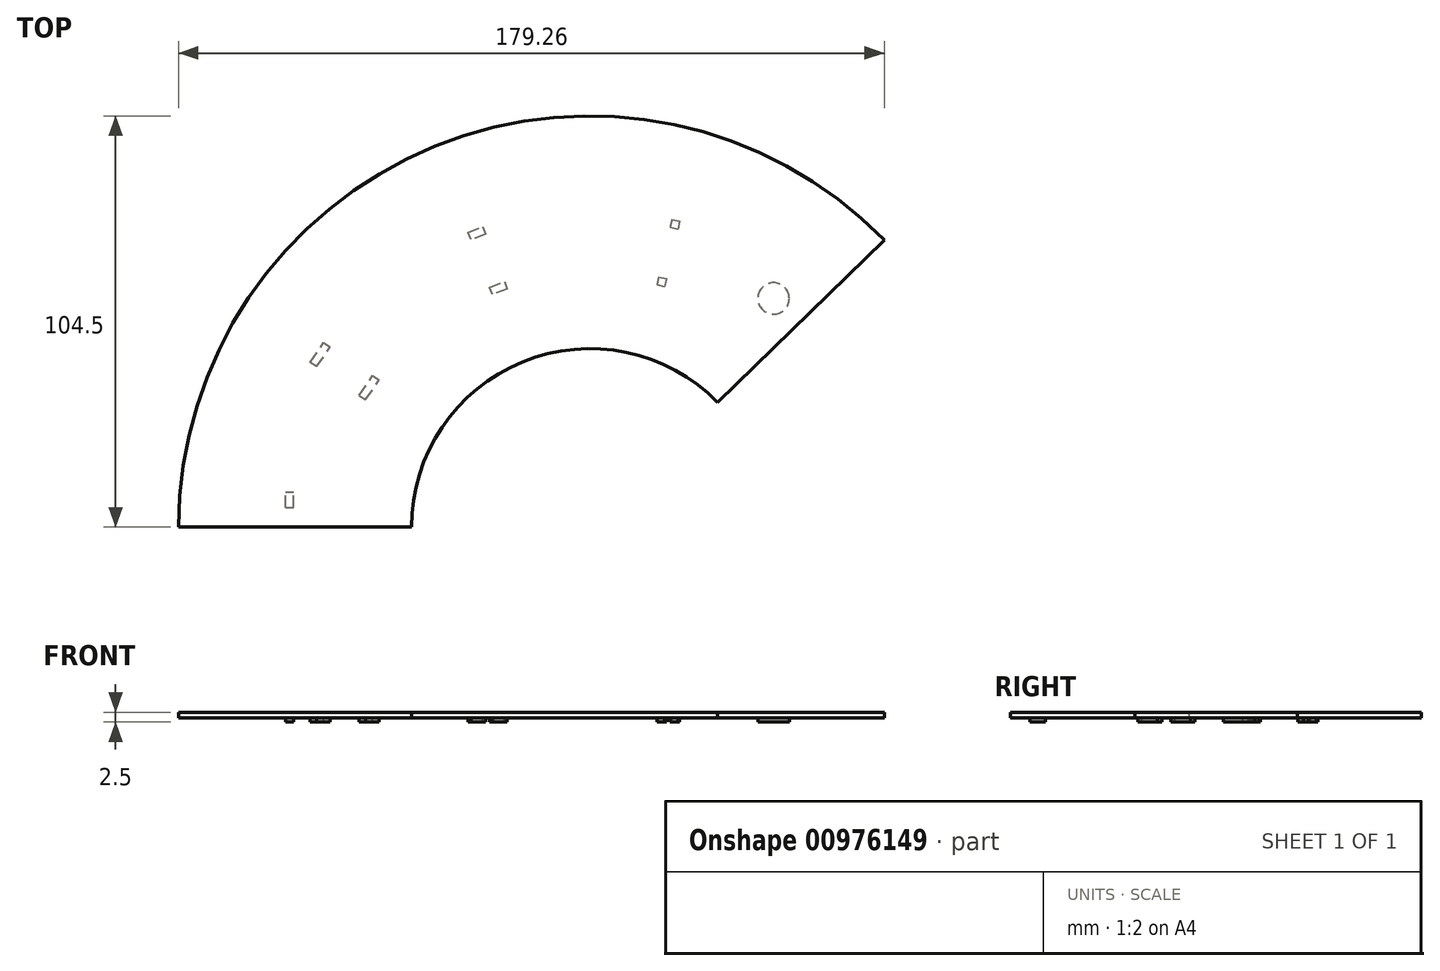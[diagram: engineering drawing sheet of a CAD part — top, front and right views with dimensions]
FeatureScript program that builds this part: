
annotation { "Feature Type Name" : "Feature", "Feature Type Description" : "" }
export const myFeature = defineFeature(function(context is Context, id is Id, definition is map)
    precondition{}
    {
        {
            var Q0;
            Q0=qCreatedBy(makeId("Top.planeOp"),FACE);
            var sketch = newSketch(context, id + "F0", { "sketchPlane" : qUnion([Q0])});
            skArc(sketch, "E0", {"start": v(74.76, 73.01) * mm, "mid": v(-39.42, 96.78) * mm, "end": v(-104.5, 0) * mm});
            skArc(sketch, "E1", {"start": v(32.44, 31.69) * mm, "mid": v(-17.1, 42) * mm, "end": v(-45.35, 0) * mm});
            skLineSegment(sketch, "E2", {"start": v(-45.35, 0) * mm, "end": v(-104.5, 0) * mm});
            skLineSegment(sketch, "E3", {"start": v(32.44, 31.69) * mm, "end": v(74.76, 73.01) * mm});
            skSolve(sketch);
        }
        {
            var Q0;
            Q0=qSketchRegion(id+"F0",true);
            extrude(context, id + "F1", {"entities" : qUnion([Q0]), "depth" : 1.5 * mm, "offsetDistance" : 25 * mm});
        }
        {
            var Q0;
            Q0=makeQuery(id+"F1.opExtrude","CAP_FACE",FACE,{"disambiguationData":[OSD([sQuery(id+"F0.wireOp",EDGE,"E0"),sQuery(id+"F0.wireOp",EDGE,"E1"),sQuery(id+"F0.wireOp",EDGE,"E2"),sQuery(id+"F0.wireOp",EDGE,"E3")])],"isStart":false});
            var sketch = newSketch(context, id + "F2", { "sketchPlane" : qUnion([Q0])});
            skLineSegment(sketch, "E4", {"start": v(-17.1, 42) * mm, "end": v(-39.42, 96.78) * mm});
            skLineSegment(sketch, "E5", {"start": v(-38.13, 24.55) * mm, "end": v(-87.2, 57.58) * mm});
            skLineSegment(sketch, "E6", {"start": v(10.49, 44.12) * mm, "end": v(22.52, 102.04) * mm});
            skLineSegment(sketch, "E7", {"start": v(-54.72, 35.71) * mm, "end": v(-55.84, 34.05) * mm});
            skLineSegment(sketch, "E8", {"start": v(-55.84, 34.05) * mm, "end": v(-57.5, 35.17) * mm});
            skLineSegment(sketch, "E9", {"start": v(-57.5, 35.17) * mm, "end": v(-56.38, 36.83) * mm});
            skLineSegment(sketch, "E10", {"start": v(-56.38, 36.83) * mm, "end": v(-55.27, 38.49) * mm});
            skLineSegment(sketch, "E11", {"start": v(-55.27, 38.49) * mm, "end": v(-53.6, 37.37) * mm});
            skLineSegment(sketch, "E12", {"start": v(-54.72, 35.71) * mm, "end": v(-53.6, 37.37) * mm});
            skLineSegment(sketch, "E13", {"start": v(-67.17, 44.09) * mm, "end": v(-68.29, 42.43) * mm});
            skLineSegment(sketch, "E14", {"start": v(-68.29, 42.43) * mm, "end": v(-69.94, 43.55) * mm});
            skLineSegment(sketch, "E15", {"start": v(-69.94, 43.55) * mm, "end": v(-68.83, 45.2) * mm});
            skLineSegment(sketch, "E16", {"start": v(-68.83, 45.2) * mm, "end": v(-67.71, 46.86) * mm});
            skLineSegment(sketch, "E17", {"start": v(-67.71, 46.86) * mm, "end": v(-66.05, 45.75) * mm});
            skLineSegment(sketch, "E18", {"start": v(-67.17, 44.09) * mm, "end": v(-66.05, 45.75) * mm});
            skLineSegment(sketch, "E19.1.0", {"start": v(-30.98, 74.88) * mm, "end": v(-29.12, 75.62) * mm});
            skLineSegment(sketch, "E19.1.1", {"start": v(-29.12, 75.62) * mm, "end": v(-27.26, 76.35) * mm});
            skLineSegment(sketch, "E19.1.2", {"start": v(-28.39, 73.76) * mm, "end": v(-26.53, 74.5) * mm});
            skLineSegment(sketch, "E19.1.3", {"start": v(-27.26, 76.35) * mm, "end": v(-26.53, 74.5) * mm});
            skLineSegment(sketch, "E19.1.4", {"start": v(-28.39, 73.76) * mm, "end": v(-30.25, 73.02) * mm});
            skLineSegment(sketch, "E19.1.5", {"start": v(-30.25, 73.02) * mm, "end": v(-30.98, 74.88) * mm});
            skLineSegment(sketch, "E19.1.6", {"start": v(-25.47, 60.93) * mm, "end": v(-23.6, 61.67) * mm});
            skLineSegment(sketch, "E19.1.7", {"start": v(-23.6, 61.67) * mm, "end": v(-21.75, 62.4) * mm});
            skLineSegment(sketch, "E19.1.8", {"start": v(-21.75, 62.4) * mm, "end": v(-21.01, 60.54) * mm});
            skLineSegment(sketch, "E19.1.9", {"start": v(-22.87, 59.8) * mm, "end": v(-21.01, 60.54) * mm});
            skLineSegment(sketch, "E19.1.10", {"start": v(-22.87, 59.8) * mm, "end": v(-24.73, 59.07) * mm});
            skLineSegment(sketch, "E19.1.11", {"start": v(-24.73, 59.07) * mm, "end": v(-25.47, 60.93) * mm});
            skLineSegment(sketch, "E19.2.1", {"start": v(20.83, 78.2) * mm, "end": v(22.78, 77.75) * mm});
            skLineSegment(sketch, "E19.2.2", {"start": v(20.38, 76.25) * mm, "end": v(22.33, 75.8) * mm});
            skLineSegment(sketch, "E19.2.3", {"start": v(22.78, 77.75) * mm, "end": v(22.33, 75.8) * mm});
            skLineSegment(sketch, "E19.2.7", {"start": v(17.47, 63.58) * mm, "end": v(19.42, 63.13) * mm});
            skLineSegment(sketch, "E19.2.8", {"start": v(19.42, 63.13) * mm, "end": v(18.97, 61.18) * mm});
            skLineSegment(sketch, "E19.2.9", {"start": v(17.02, 61.63) * mm, "end": v(18.97, 61.18) * mm});
            skPoint(sketch, "E19.center", {"position": v(0, -3.52) * mm});
            skLineSegment(sketch, "E19.anchor1", {"start": v(0, -3.52) * mm, "end": v(-69.94, 43.55) * mm, "construction": true});
            skLineSegment(sketch, "E19.anchor2", {"start": v(0, -3.52) * mm, "end": v(18.51, 77.06) * mm, "construction": true});
            skLineSegment(sketch, "E20", {"start": v(17.47, 63.58) * mm, "end": v(17.02, 61.63) * mm});
            skLineSegment(sketch, "E21", {"start": v(20.83, 78.2) * mm, "end": v(20.38, 76.25) * mm});
            skLineSegment(sketch, "E22", {"start": v(-68.29, 42.43) * mm, "end": v(-69.4, 40.77) * mm});
            skLineSegment(sketch, "E23", {"start": v(-69.4, 40.77) * mm, "end": v(-71.06, 41.89) * mm});
            skLineSegment(sketch, "E24", {"start": v(-71.06, 41.89) * mm, "end": v(-69.94, 43.55) * mm});
            skLineSegment(sketch, "E25", {"start": v(-57.5, 35.17) * mm, "end": v(-58.62, 33.51) * mm});
            skLineSegment(sketch, "E26", {"start": v(-58.62, 33.51) * mm, "end": v(-56.96, 32.4) * mm});
            skLineSegment(sketch, "E27", {"start": v(-56.96, 32.4) * mm, "end": v(-55.84, 34.05) * mm});
            skLineSegment(sketch, "E28.bottom", {"start": v(-77.35, 5) * mm, "end": v(-75.35, 5) * mm});
            skLineSegment(sketch, "E28.top", {"start": v(-77.35, 9) * mm, "end": v(-75.35, 9) * mm});
            skLineSegment(sketch, "E28.left", {"start": v(-77.35, 5) * mm, "end": v(-77.35, 9) * mm});
            skLineSegment(sketch, "E28.right", {"start": v(-75.35, 5) * mm, "end": v(-75.35, 9) * mm});
            skCircle(sketch, "E29", {"center": v(46.63, 58.12) * mm, "radius": 4 * mm});
            skSolve(sketch);
        }
        {
            var Q0;
            Q0=qSketchRegion(id+"F2",true);
            extrude(context, id + "F3", {"entities" : qUnion([Q0]), "operationType" : NewBodyOperationType.ADD, "oppositeDirection" : true, "depth" : 2.5 * mm, "offsetDistance" : 25 * mm});
        }
    });
